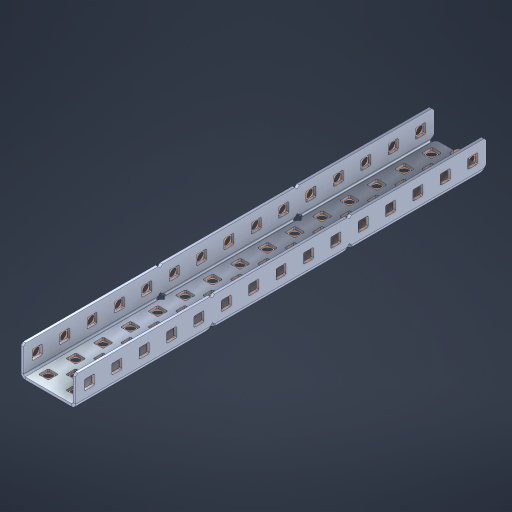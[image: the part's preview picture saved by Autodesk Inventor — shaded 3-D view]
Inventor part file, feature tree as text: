
AUTODESK INVENTOR PART (.ipt)
format: ipt  version: 2023 (Build 270158000, 158)  size: 1,155,584 bytes
history: native  units: in
note: dims shown in document units (in); Inventor stores cm internally (conversion verified against a paired STEP export)
features: other x82, extrude x73, sheet_metal_op x11, sketch x10, pattern_linear x2, mirror x1, chamfer x1
ambient origin geometry x8: Origin, YZ Plane, XZ Plane, XY Plane, X Axis, Y Axis, Z Axis, Center Point
bodies: Solid1 (feature_tree), Body (feature_tree)
feature tree (180):
  sheet_metal_op  "Flanges"
  other  "Flange Pattern Plane"
  other  "Flange Pattern Sketch"
  sheet_metal_op  "Flange Pattern"
  sheet_metal_op  "Body Pattern"
  pattern_linear  "Center Pattern"  Spacing1=0.0469in  [1 undecoded]
  other  "Arc Length"
  mirror  "Notch Mirror"
  pattern_linear  "Notch Pattern"  Spacing1=0.182in  [1 undecoded]
  chamfer  "End Chamfer"
  extrude  "Half Cut"  Depth=0.02in
  sketch  "Sketch1"  dims[d0=1.0in]
  other  "Plate1"
  sketch  "Sketch2"  dims[d1=7.5in]
  other  "Plate2"
  sheet_metal_op  "Bend1"
  sheet_metal_op  "Corner1"
  sketch  "Sketch3"  dims[d2=0.0469in]
  sketch  "Sketch7"  dims[d3=0.0469in]
  other  "Srf1"
  other  "Srf2"
  sketch  "Sketch8"  dims[d4=0.0234in]
  sketch  "Sketch9"  dims[d5=0.0938in]
  other  "Srf91"
  sheet_metal_op  "Body Pattern Sketch"
  other  "Srf92"
  sketch  "Sketch13"  dims[d6=0.0469in]
  sketch  "Sketch14"  dims[d7=0.5in d8=90.0deg d9=0.0312in]
  sketch  "Sketch15"  dims[d10=0.1875in]
  sketch  "Sketch16"  dims[d11=0.0469in d12=0.0469in d16=0.182in d17=0.02in d18=0.0469in d19=0.0in d20=0.25in d21=0.25in d38=5.9055in d40=0.5in d41=0.7874in d43=1.0in d46=0.172in d47=1.0in d48=0.0in d49=0.182in d50=0.02in d51=0.25in d52=0.25in d53=0.0469in d54=0.0in d55=0.172in d56=1.0in d57=0.0in d58=0.25in d60=5.9055in d62=0.5in d63=0.7874in d65=0.5in d85=0.1227in d86=0.1659in d88=0.04in d89=0.0469in d90=0.0in d91=0.04in d92=0.0491in d95=2.5in d96=0.04in d97=0.25in d98=45.0deg d99=0.25in d100=0.5in d101=0.0in d102=2.497in d106=0.182in d107=0.02in d108=0.5in d109=0.5in d110=0.0469in d111=0.0in d112=0.172in d113=0.5in d114=0.0in d117=0.5in d118=0.5in d119=0.5in]
  other  "Srf786"
  other  "Srf823"
  other  "Srf824"
  other  "Srf825"
  other  "Srf826"
  other  "Srf827"
  other  "Srf828"
  other  "Srf829"
  other  "Srf856"
  other  "Srf857"
  other  "Srf858"
  other  "Srf859"
  other  "Srf860"
  other  "Srf861"
  other  "Srf862"
  other  "Srf889"
  other  "Srf890"
  other  "Srf891"
  other  "Srf892"
  other  "Srf893"
  other  "Srf894"
  other  "Srf895"
  other  "Srf896"
  other  "Srf922"
  other  "Srf923"
  other  "Srf924"
  other  "Srf925"
  other  "Srf926"
  other  "Srf959"
  other  "Srf960"
  other  "Srf961"
  other  "Srf962"
  other  "Srf963"
  other  "Srf996"
  other  "Srf997"
  other  "Srf998"
  other  "Srf999"
  other  "Srf1000"
  other  "Srf1143"
  other  "Srf1144"
  other  "Srf1145"
  other  "Srf1146"
  other  "Srf1147"
  other  "Srf1148"
  other  "Srf1149"
  other  "Srf1150"
  other  "Srf1151"
  other  "Srf1152"
  other  "Srf1153"
  other  "Srf1154"
  other  "Srf1155"
  other  "Srf1156"
  other  "Srf1157"
  other  "Srf1158"
  other  "Srf1199"
  other  "Srf1200"
  other  "Srf1201"
  other  "Srf1202"
  other  "Srf1203"
  other  "Srf1204"
  other  "Srf1205"
  other  "Srf1206"
  other  "Srf1207"
  other  "Srf1208"
  other  "Srf1209"
  other  "Srf1210"
  other  "Srf1211"
  other  "Srf1212"
  other  "Srf1213"
  other  "Srf1214"
  other  "Srf1255"
  sheet_metal_op  "Flange Stamp"
  sheet_metal_op  "Flange Circle"
  sheet_metal_op  "Body Stamp"
  sheet_metal_op  "Body Circle"
  other  "Center Stamp"
  other  "Center Circle"
  sheet_metal_op  "Notch"
  extrude  "ExtrusionSrf2"  Depth=0.0469in
  extrude  "ExtrusionSrf92"  TaperAngle=0.0deg  [1 undecoded]
  extrude  "ExtrusionSrf823"  Depth=0.5in
  extrude  "ExtrusionSrf824"  Depth=0.5in
  extrude  "ExtrusionSrf825"  Depth=0.5in
  extrude  "ExtrusionSrf826"  Depth=0.5in
  extrude  "ExtrusionSrf827"  Depth=1.0in TaperAngle=0.0deg
  extrude  "ExtrusionSrf828"  Depth=0.5in
  extrude  "ExtrusionSrf829"  Depth=0.02in
  extrude  "ExtrusionSrf856"  Depth=0.5in
  extrude  "ExtrusionSrf857"  Depth=0.5in
  extrude  "ExtrusionSrf858"  Depth=0.0469in
  extrude  "ExtrusionSrf859"  TaperAngle=0.0deg  [1 undecoded]
  extrude  "ExtrusionSrf860"  Depth=0.5in
  extrude  "ExtrusionSrf861"  Depth=1.0in TaperAngle=0.0deg
  extrude  "ExtrusionSrf862"  Depth=0.5in
  extrude  "ExtrusionSrf889"  Depth=0.5in
  extrude  "ExtrusionSrf890"  Depth=0.5in
  extrude  "ExtrusionSrf891"  Depth=0.5in
  extrude  "ExtrusionSrf892"  Depth=0.5in
  extrude  "ExtrusionSrf893"  Depth=0.5in
  extrude  "ExtrusionSrf894"  Depth=0.0469in
  extrude  "ExtrusionSrf895"  TaperAngle=0.0deg  [1 undecoded]
  extrude  "ExtrusionSrf896"  Depth=0.5in
  extrude  "ExtrusionSrf922"  Depth=0.5in
  extrude  "ExtrusionSrf923"  Depth=2.5in
  extrude  "ExtrusionSrf924"  Depth=0.5in TaperAngle=45.0deg
  extrude  "ExtrusionSrf925"  Depth=0.5in
  extrude  "ExtrusionSrf926"  Depth=0.5in TaperAngle=0.0deg
  extrude  "ExtrusionSrf959"  Depth=0.5in
  extrude  "ExtrusionSrf960"  Depth=0.5in
  extrude  "ExtrusionSrf961"  Depth=0.02in
  extrude  "ExtrusionSrf962"  Depth=0.5in
  extrude  "ExtrusionSrf963"  Depth=0.5in
  extrude  "ExtrusionSrf996"  Depth=0.0469in
  extrude  "ExtrusionSrf997"  TaperAngle=0.0deg  [1 undecoded]
  extrude  "ExtrusionSrf998"  Depth=0.5in
  extrude  "ExtrusionSrf999"  Depth=0.5in TaperAngle=0.0deg
  extrude  "ExtrusionSrf1000"  Depth=0.5in
  extrude  "ExtrusionSrf1143"  Depth=0.5in
  extrude  "ExtrusionSrf1144"  Depth=0.5in
  extrude  "ExtrusionSrf1145"  [1 undecoded]
  extrude  "ExtrusionSrf1146"  [1 undecoded]
  extrude  "ExtrusionSrf1147"  [1 undecoded]
  extrude  "ExtrusionSrf1148"  [1 undecoded]
  extrude  "ExtrusionSrf1149"  [1 undecoded]
  extrude  "ExtrusionSrf1150"  [1 undecoded]
  extrude  "ExtrusionSrf1151"  [1 undecoded]
  extrude  "ExtrusionSrf1152"  [1 undecoded]
  extrude  "ExtrusionSrf1153"  [1 undecoded]
  extrude  "ExtrusionSrf1154"  [1 undecoded]
  extrude  "ExtrusionSrf1155"  [1 undecoded]
  extrude  "ExtrusionSrf1156"  [1 undecoded]
  extrude  "ExtrusionSrf1157"  [1 undecoded]
  extrude  "ExtrusionSrf1158"  [1 undecoded]
  extrude  "ExtrusionSrf1199"  [1 undecoded]
  extrude  "ExtrusionSrf1200"  [1 undecoded]
  extrude  "ExtrusionSrf1201"  [1 undecoded]
  extrude  "ExtrusionSrf1202"  [1 undecoded]
  extrude  "ExtrusionSrf1203"  [1 undecoded]
  extrude  "ExtrusionSrf1204"  [1 undecoded]
  extrude  "ExtrusionSrf1205"  [1 undecoded]
  extrude  "ExtrusionSrf1206"  [1 undecoded]
  extrude  "ExtrusionSrf1207"  [1 undecoded]
  extrude  "ExtrusionSrf1208"  [1 undecoded]
  extrude  "ExtrusionSrf1209"  [1 undecoded]
  extrude  "ExtrusionSrf1210"  [1 undecoded]
  extrude  "ExtrusionSrf1211"  [1 undecoded]
  extrude  "ExtrusionSrf1212"  [1 undecoded]
  extrude  "ExtrusionSrf1213"  [1 undecoded]
  extrude  "ExtrusionSrf1214"  [1 undecoded]
  extrude  "ExtrusionSrf1255"  [1 undecoded]
note: 37 required parameter values undecoded (feature->parameter linkage not recoverable at this tier; creation-order binding heuristic only, values carry confidence <= 0.55)
